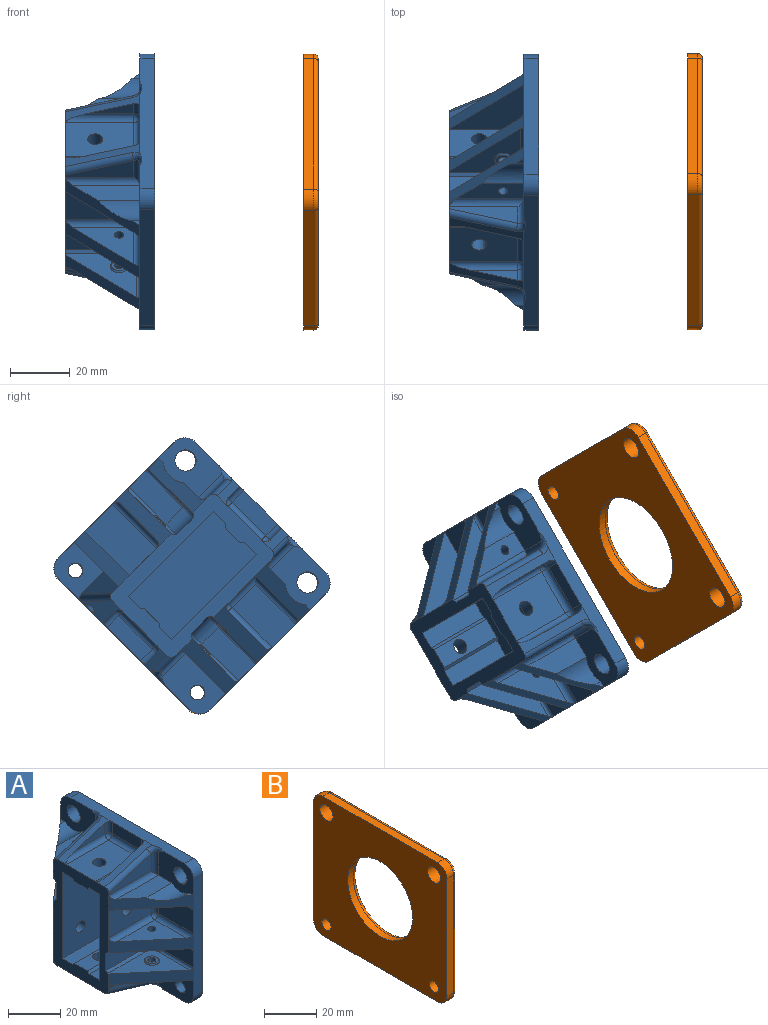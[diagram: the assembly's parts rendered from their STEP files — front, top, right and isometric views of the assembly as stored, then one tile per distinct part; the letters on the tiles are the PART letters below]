
ASSEMBLY  parts=2 mates=1
PART A: 143 faces, bbox 33.4x74.8x68.7 mm
  f0: plane 2.67x2.25mm, normal (0,0,1), area 3mm2, adj f7,f73,f135
  f1: plane 22.62x7.25mm, normal (0,0,1), area 132.6mm2, adj f7,f73,f126,f135
  f2: plane 22.62x7.25mm, normal (0,0,1), area 125.1mm2, adj f16,f68,f83,f130,f134
  f3: plane 2.67x2.25mm, normal (0,0,1), area 3mm2, adj f16,f68,f134
  f4: plane 16x5.5mm, normal (-1,0,0), area 88mm2, adj f23,f109,f112,f113
  f5: plane 23x16mm, normal (0,0,-1), area 347.6mm2, adj f19,f90,f110,f113,f115
  f6: plane 16.35x12.94mm, normal (-1,0,0), area 150.6mm2, adj f23,f24,f28,f32,f58,f131,f142
  f7: plane 19.54x14.74mm, normal (-1,0,0), area 201.8mm2, adj f0,f1,f21,f22,f26,f30,f125,f135
  f8: plane 23x16mm, normal (0,0,1), area 347.6mm2, adj f19,f91,f116,f119,f122
  f9: plane 16x5.5mm, normal (-1,0,0), area 88mm2, adj f21,f117,f119,f120
  f10: plane 17.5x8mm, normal (-1,0,0), area 140mm2, adj f22,f95,f96,f100
  f11: plane 17.5x8mm, normal (-1,0,0), area 140mm2, adj f24,f94,f98,f102
  f12: plane 19x11mm, normal (-1,0,0), area 209mm2, adj f22,f104,f107,f108
  f13: plane 23x13mm, normal (0,-1,0), area 278.6mm2, adj f19,f61,f92,f105,f108
  f14: plane 19.54x13.04mm, normal (-1,0,0), area 210.8mm2, adj f22,f23,f29,f31,f60,f127,f141
  f15: plane 23x7.81mm, normal (0,-1,0), area 100.3mm2, adj f19,f127,f128,f140
  f16: plane 19.54x14.74mm, normal (-1,0,0), area 201.8mm2, adj f2,f3,f21,f24,f27,f33,f129,f134
  f17: plane 25x13mm, normal (0,1,0), area 304.6mm2, adj f19,f20,f59,f93,f124
  f18: plane 23x7.81mm, normal (0,1,0), area 100.3mm2, adj f19,f129,f130,f138
  f19: plane 50.44x30.44mm, normal (-1,0,0), area 654.3mm2, adj f5,f8,f13,f15,f17,f18,f34,f35
  f20: plane 21x13mm, normal (-1,0,0), area 273mm2, adj f17,f24,f59,f123
  f21: plane 63.75x6.75mm, normal (0,0,1), area 305.3mm2, adj f7,f9,f16,f25,f30,f33,f76,f77
  f22: plane 55x5mm, normal (0,-1,0), area 275mm2, adj f7,f10,f12,f14,f25,f30,f31,f71
  f23: plane 63.75x6.75mm, normal (0,0,-1), area 307.7mm2, adj f4,f6,f14,f25,f31,f32,f74,f75
  f24: plane 55x5mm, normal (0,1,0), area 275mm2, adj f6,f11,f16,f20,f25,f32,f33,f68
  f25: plane 72x65mm, normal (1,0,0), area 4539.1mm2, adj f21,f22,f23,f24,f26,f27,f28,f29
  f26: cylinder r=3.56mm len=7.13mm, axis (1,0,0), area 112mm2, adj f7,f25
  f27: cylinder r=3.56mm len=7.13mm, axis (1,0,0), area 112mm2, adj f16,f25
  f28: cylinder r=2.51mm len=5.02mm, axis (1,0,0), area 78.9mm2, adj f6,f25
  f29: cylinder r=2.51mm len=5.02mm, axis (1,0,0), area 78.9mm2, adj f14,f25
  f30: cylinder r=5mm len=5mm, axis (1,0,0), area 39.3mm2, adj f7,f21,f22,f25
  f31: cylinder r=5mm len=5mm, axis (-1,0,0), area 39.3mm2, adj f14,f22,f23,f25
  f32: cylinder r=5mm len=5mm, axis (1,0,0), area 39.3mm2, adj f6,f23,f24,f25
  f33: cylinder r=5mm len=5mm, axis (-1,0,0), area 39.3mm2, adj f16,f21,f24,f25
  f34: plane 21.93x1mm, normal (0,-0.71,-0.71), area 30.5mm2, adj f19,f35,f44,f97
  f35: plane 24x20.66mm, normal (0,0,-1), area 222.2mm2, adj f19,f34,f72,f86,f96,f97
  f36: plane 23x7.81mm, normal (0,-1,0), area 100.3mm2, adj f19,f125,f126,f136
  f37: plane 24x20.66mm, normal (0,0,-1), area 222.2mm2, adj f19,f38,f68,f79,f102,f103
  f38: plane 21.93x1mm, normal (0,0.71,-0.71), area 30.5mm2, adj f19,f37,f39,f103
  f39: plane 20x8mm, normal (0,1,0), area 160mm2, adj f19,f38,f40,f94
  f40: plane 21.93x1mm, normal (0,0.71,0.71), area 30.5mm2, adj f19,f39,f41,f99
  f41: plane 24x20.66mm, normal (0,0,1), area 222.2mm2, adj f19,f40,f69,f81,f98,f99
  f42: plane 24x20.66mm, normal (0,0,1), area 222.2mm2, adj f19,f43,f71,f87,f100,f101
  f43: plane 21.93x1mm, normal (0,-0.71,0.71), area 30.5mm2, adj f19,f42,f44,f101
  f44: plane 20x8mm, normal (0,-1,0), area 160mm2, adj f19,f34,f43,f95
  f45: plane 40.5x25mm, normal (0,1,0), area 992.1mm2, adj f19,f46,f52,f53,f92
  f46: plane 25x5.75mm, normal (0,0,-1), area 143.8mm2, adj f19,f45,f53,f57
  f47: plane 25x7mm, normal (0,0,-1), area 154.6mm2, adj f19,f53,f56,f57,f91
  f48: plane 25x5.75mm, normal (0,0,-1), area 143.8mm2, adj f19,f49,f53,f56
  f49: plane 40.5x25mm, normal (0,-1,0), area 992.1mm2, adj f19,f48,f50,f53,f93
  f50: plane 25x5.75mm, normal (0,0,1), area 143.8mm2, adj f19,f49,f53,f54
  f51: plane 25x7mm, normal (0,0,1), area 154.6mm2, adj f19,f53,f54,f55,f90
  f52: plane 25x5.75mm, normal (0,0,1), area 143.8mm2, adj f19,f45,f53,f55
  f53: plane 40.5x20.5mm, normal (-1,0,0), area 814.3mm2, adj f45,f46,f47,f48,f49,f50,f51,f52
  f54: plane 25x1mm, normal (0,0.71,0.71), area 35.4mm2, adj f19,f50,f51,f53
  f55: plane 25x1mm, normal (0,-0.71,0.71), area 35.4mm2, adj f19,f51,f52,f53
  f56: plane 25x1mm, normal (0,0.71,-0.71), area 35.4mm2, adj f19,f47,f48,f53
  f57: plane 25x1mm, normal (0,-0.71,-0.71), area 35.4mm2, adj f19,f46,f47,f53
  f58: plane 25x21mm, normal (0,0,-1), area 175mm2, adj f6,f70,f131
  f59: plane 25x21mm, normal (0,0,1), area 262.5mm2, adj f17,f20,f70
  f60: plane 22.62x19mm, normal (0,0,-1), area 207.3mm2, adj f14,f71,f88,f128
  f61: plane 23x19.32mm, normal (0,0,-1), area 222.2mm2, adj f13,f73,f107
  f62: plane 20.62x17.32mm, normal (0,0,-1), area 171mm2, adj f69,f82,f123,f124
  f63: plane 20.62x17.32mm, normal (0,0,1), area 171mm2, adj f72,f89,f104,f105
  f64: plane 16.33x4.9mm, normal (0,-1,0), area 40mm2, adj f76,f116,f117
  f65: plane 16.33x4.9mm, normal (0,1,0), area 40mm2, adj f77,f120,f122
  f66: plane 16.33x4.9mm, normal (0,-1,0), area 40mm2, adj f74,f109,f110
  f67: plane 16.33x4.9mm, normal (0,1,0), area 40mm2, adj f75,f112,f115
  f68: plane 26x22mm, normal (-0.64,0.77,0), area 147.7mm2, adj f2,f3,f19,f24,f37,f102,f130,f134
  f69: plane 26x22mm, normal (-0.64,0.77,0), area 166mm2, adj f19,f24,f41,f62,f98,f123,f124
  f70: plane 25x21mm, normal (-0.64,0.77,0), area 163.2mm2, adj f19,f24,f58,f59
  f71: plane 26x22mm, normal (-0.64,-0.77,0), area 164.9mm2, adj f19,f22,f42,f60,f100,f128
  f72: plane 26x22mm, normal (-0.64,-0.77,0), area 166mm2, adj f19,f22,f35,f63,f96,f104,f105
  f73: plane 26x22mm, normal (-0.64,-0.77,0), area 148.5mm2, adj f0,f1,f19,f22,f61,f107,f126,f135
  f74: plane 27.8x14.89mm, normal (-0.29,0,-0.96), area 161.9mm2, adj f19,f23,f66,f109,f110,f132,f142
  f75: plane 27.8x10.3mm, normal (-0.29,0,-0.96), area 83mm2, adj f19,f23,f67,f112,f115,f140,f141
  f76: plane 27.8x10.3mm, normal (-0.29,0,0.96), area 83mm2, adj f19,f21,f64,f116,f117,f138,f139
  f77: plane 27.8x10.3mm, normal (-0.29,0,0.96), area 83mm2, adj f19,f21,f65,f120,f122,f136,f137
  f78: plane 5x5mm, normal (0,0,-1), area 12.1mm2, adj f79,f83
  f79: cone r=2.5mm half-angle=45deg, axis (0,0,1), area 12.2mm2, adj f37,f78
  f80: plane 5x5mm, normal (0,0,1), area 12.1mm2, adj f81,f82
  f81: cone r=2.5mm half-angle=45deg, axis (0,0,-1), area 12.2mm2, adj f41,f80
  f82: cylinder r=1.55mm len=5.5mm, axis (0,0,1), area 53.6mm2, adj f62,f80
  f83: cylinder r=1.55mm len=5.5mm, axis (0,0,1), area 53.6mm2, adj f2,f78
  f84: plane 5x5mm, normal (0,0,-1), area 12.1mm2, adj f86,f89
  f85: plane 5x5mm, normal (0,0,1), area 12.1mm2, adj f87,f88
  f86: cone r=2.5mm half-angle=45deg, axis (0,0,1), area 12.2mm2, adj f35,f84
  f87: cone r=2.5mm half-angle=45deg, axis (0,0,-1), area 12.2mm2, adj f42,f85
  f88: cylinder r=1.55mm len=5.5mm, axis (0,0,-1), area 53.6mm2, adj f60,f85
  f89: cylinder r=1.55mm len=5.5mm, axis (0,0,-1), area 53.6mm2, adj f63,f84
  f90: cylinder r=2.55mm len=5.75mm, axis (0,0,1), area 92.1mm2, adj f5,f51
  f91: cylinder r=2.55mm len=5.75mm, axis (0,0,1), area 92.1mm2, adj f8,f47
  f92: cylinder r=2.55mm len=5.1mm, axis (0,-1,0), area 76.1mm2, adj f13,f45
  f93: cylinder r=2.55mm len=5.1mm, axis (0,1,0), area 76.1mm2, adj f17,f49
  f94: cylinder r=5mm len=8mm, axis (0,0,1), area 62.8mm2, adj f11,f39,f99,f103
  f95: cylinder r=5mm len=8mm, axis (0,0,-1), area 62.8mm2, adj f10,f44,f97,f101
  f96: cylinder r=1mm len=17.5mm, axis (0,1,0), area 26.8mm2, adj f10,f35,f72,f97
  f97: torus R=4mm, axis (0,0,1), area 9mm2, adj f34,f35,f95,f96
  f98: cylinder r=1mm len=17.5mm, axis (0,-1,0), area 26.8mm2, adj f11,f41,f69,f99
  f99: torus R=4mm, axis (0,0,-1), area 9mm2, adj f40,f41,f94,f98
  f100: cylinder r=1mm len=17.5mm, axis (0,-1,0), area 26.8mm2, adj f10,f42,f71,f101
  f101: torus R=4mm, axis (0,0,-1), area 9mm2, adj f42,f43,f95,f100
  f102: cylinder r=1mm len=17.5mm, axis (0,1,0), area 26.8mm2, adj f11,f37,f68,f103
  f103: torus R=4mm, axis (0,0,1), area 9mm2, adj f37,f38,f94,f102
  f104: cylinder r=2mm len=19mm, axis (0,-1,0), area 57.1mm2, adj f12,f63,f72,f106
  f105: cylinder r=2mm len=23mm, axis (1,0,0), area 68.5mm2, adj f13,f63,f72,f106
  f106: sphere r=2mm, area 4mm2, adj f104,f105,f108
  f107: cylinder r=2mm len=21mm, axis (0,1,0), area 60.2mm2, adj f12,f61,f73,f108
  f108: cylinder r=2mm len=13mm, axis (0,0,-1), area 37.7mm2, adj f12,f13,f106,f107
  f109: cylinder r=2mm len=5.5mm, axis (0,0,-1), area 16.3mm2, adj f4,f66,f74,f111
  f110: cylinder r=2mm len=23mm, axis (1,0,0), area 61.8mm2, adj f5,f66,f74,f111
  f111: sphere r=2mm, area 4mm2, adj f109,f110,f113
  f112: cylinder r=2mm len=5.5mm, axis (0,0,1), area 16.3mm2, adj f4,f67,f75,f114
  f113: cylinder r=2mm len=16mm, axis (0,1,0), area 50.3mm2, adj f4,f5,f111,f114
  f114: sphere r=2mm, area 6.3mm2, adj f112,f113,f115
  f115: cylinder r=2mm len=23mm, axis (-1,0,0), area 61.8mm2, adj f5,f67,f75,f114
  f116: cylinder r=2mm len=23mm, axis (1,0,0), area 61.8mm2, adj f8,f64,f76,f118
  f117: cylinder r=2mm len=5.5mm, axis (0,0,-1), area 16.3mm2, adj f9,f64,f76,f118
  f118: sphere r=2mm, area 4mm2, adj f116,f117,f119
  f119: cylinder r=2mm len=16mm, axis (0,-1,0), area 50.3mm2, adj f8,f9,f118,f121
  f120: cylinder r=2mm len=5.5mm, axis (0,0,1), area 16.3mm2, adj f9,f65,f77,f121
  f121: sphere r=2mm, area 8.6mm2, adj f119,f120,f122
  f122: cylinder r=2mm len=23mm, axis (-1,0,0), area 61.8mm2, adj f8,f65,f77,f121
  f123: cylinder r=2mm len=21mm, axis (0,1,0), area 60.2mm2, adj f20,f62,f69,f124
  f124: cylinder r=2mm len=25mm, axis (1,0,0), area 71.7mm2, adj f17,f62,f69,f123
  f125: cylinder r=2mm len=11.01mm, axis (0,0,-1), area 29.6mm2, adj f7,f36,f126,f137
  f126: cylinder r=2mm len=25mm, axis (1,0,0), area 71.7mm2, adj f1,f36,f73,f125
  f127: cylinder r=2mm len=11.01mm, axis (0,0,-1), area 29.6mm2, adj f14,f15,f128,f141
  f128: cylinder r=2mm len=25mm, axis (-1,0,0), area 71.7mm2, adj f15,f60,f71,f127
  f129: cylinder r=2mm len=11.01mm, axis (0,0,1), area 29.6mm2, adj f16,f18,f130,f139
  f130: cylinder r=2mm len=25mm, axis (1,0,0), area 71.7mm2, adj f2,f18,f68,f129
  f131: plane 25x10.57mm, normal (-0.27,0.96,0), area 177.2mm2, adj f6,f19,f58,f142
  f132: cylinder r=2.05mm len=12.46mm, axis (0,0,1), area 152.5mm2, adj f74,f133
  f133: plane 4.1x4.1mm, normal (0,0,-1), area 13.2mm2, adj f132
  f134: cylinder r=7.5mm len=13.99mm, axis (1,0,0), area 85.8mm2, adj f2,f3,f16,f68
  f135: cylinder r=7.5mm len=13.99mm, axis (1,0,0), area 85.8mm2, adj f0,f1,f7,f73
  f136: cylinder r=2mm len=23.57mm, axis (-0.96,0,-0.29), area 74.5mm2, adj f19,f36,f77,f137
  f137: bspline ~7.06x4mm, area 16.3mm2, adj f7,f21,f77,f125,f136
  f138: cylinder r=2mm len=23.57mm, axis (0.96,0,0.29), area 74.5mm2, adj f18,f19,f76,f139
  f139: bspline ~7.06x4mm, area 16.3mm2, adj f16,f21,f76,f129,f138
  f140: cylinder r=2mm len=23.57mm, axis (-0.96,0,0.29), area 74.5mm2, adj f15,f19,f75,f141
  f141: bspline ~7.06x4mm, area 16.3mm2, adj f14,f23,f75,f127,f140
  f142: cylinder r=2mm len=25.26mm, axis (0.93,0.26,-0.28), area 80.7mm2, adj f6,f19,f74,f131
PART B: 24 faces, bbox 5x72.8x65.8 mm
  f0: plane 55x3.5mm, normal (0,-1,0), area 192.5mm2, adj f5,f11,f14,f17
  f1: plane 62x3.5mm, normal (0,0,-1), area 217mm2, adj f5,f11,f12,f21
  f2: plane 55x3.5mm, normal (0,1,0), area 192.5mm2, adj f5,f12,f13,f22
  f3: plane 62x3.5mm, normal (0,0,1), area 217mm2, adj f5,f13,f14,f18
  f4: plane 69x62mm, normal (1,0,0), area 2953.5mm2, adj f6,f7,f8,f9,f15,f16,f17,f18
  f5: plane 72x65mm, normal (-1,0,0), area 3577mm2, adj f0,f1,f2,f3,f6,f7,f8,f9
  f6: cylinder r=3.56mm len=7.13mm, axis (1,0,0), area 112mm2, adj f4,f5
  f7: cylinder r=3.56mm len=7.13mm, axis (1,0,0), area 112mm2, adj f4,f5
  f8: cylinder r=2.51mm len=5.02mm, axis (1,0,0), area 78.9mm2, adj f4,f5
  f9: cylinder r=2.51mm len=5.02mm, axis (1,0,0), area 78.9mm2, adj f4,f5
  f10: cylinder r=17.5mm len=35mm, axis (1,0,0), area 329.9mm2, adj f5,f15
  f11: cylinder r=5mm len=5mm, axis (-1,0,0), area 27.5mm2, adj f0,f1,f5,f19
  f12: cylinder r=5mm len=5mm, axis (1,0,0), area 27.5mm2, adj f1,f2,f5,f23
  f13: cylinder r=5mm len=5mm, axis (-1,0,0), area 27.5mm2, adj f2,f3,f5,f20
  f14: cylinder r=5mm len=5mm, axis (1,0,0), area 27.5mm2, adj f0,f3,f5,f16
  f15: torus R=19.5mm, axis (1,0,0), area 359.8mm2, adj f4,f10
  f16: torus R=3.5mm, axis (1,0,0), area 16.5mm2, adj f4,f14,f17,f18
  f17: cylinder r=1.5mm len=55mm, axis (0,0,1), area 129.6mm2, adj f0,f4,f16,f19
  f18: cylinder r=1.5mm len=62mm, axis (0,1,0), area 146.1mm2, adj f3,f4,f16,f20
  f19: torus R=3.5mm, axis (1,0,0), area 16.5mm2, adj f4,f11,f17,f21
  f20: torus R=3.5mm, axis (1,0,0), area 16.5mm2, adj f4,f13,f18,f22
  f21: cylinder r=1.5mm len=62mm, axis (0,-1,0), area 146.1mm2, adj f1,f4,f19,f23
  f22: cylinder r=1.5mm len=55mm, axis (0,0,-1), area 129.6mm2, adj f2,f4,f20,f23
  f23: torus R=3.5mm, axis (1,0,0), area 16.5mm2, adj f4,f12,f21,f22
PLACE A rot(axis=(1,0,0),45deg) t=(41.07,32.12,23.6)mm
PLACE B rot(axis=(1,0,0),45deg) t=(71.07,32.28,23.44)mm
MATE fastened A.f25 <-> B.f10  axis (1,0,0) through (21.07,32.28,23.44)mm
